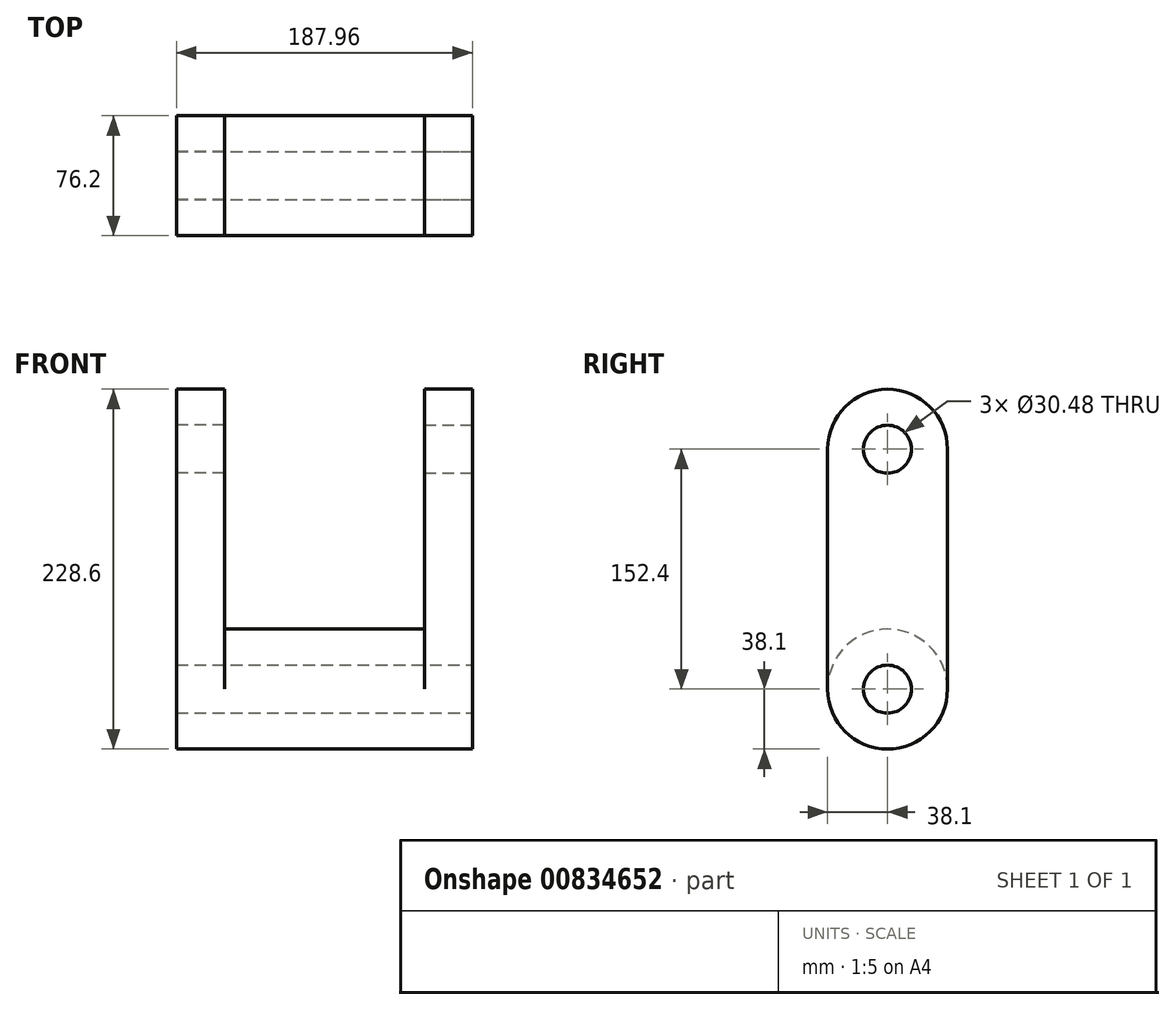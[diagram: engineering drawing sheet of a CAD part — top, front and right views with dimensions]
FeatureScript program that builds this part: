
annotation { "Feature Type Name" : "Feature", "Feature Type Description" : "" }
export const myFeature = defineFeature(function(context is Context, id is Id, definition is map)
    precondition{}
    {
        {
            var Q0;
            Q0=qCreatedBy(makeId("Right.planeOp"),FACE);
            var sketch = newSketch(context, id + "F0", { "sketchPlane" : qUnion([Q0])});
            skLineSegment(sketch, "E0.left", {"start": v(-38.1, 76.2) * mm, "end": v(-38.1, -76.2) * mm});
            skLineSegment(sketch, "E0.right", {"start": v(38.1, 76.2) * mm, "end": v(38.1, -76.2) * mm});
            skArc(sketch, "E1", {"start": v(38.1, 76.2) * mm, "mid": v(0, 114.3) * mm, "end": v(-38.1, 76.2) * mm});
            skArc(sketch, "E2", {"start": v(-38.1, -76.2) * mm, "mid": v(0, -114.3) * mm, "end": v(38.1, -76.2) * mm});
            skCircle(sketch, "E3", {"center": v(0, 76.2) * mm, "radius": 15.24 * mm});
            skCircle(sketch, "E4", {"center": v(0, -76.2) * mm, "radius": 15.24 * mm});
            skSolve(sketch);
        }
        {
            var Q0;
            Q0=makeQuery(id+"F0.imprint","IMPRINT",FACE,{"disambiguationData":[TD([[makeQuery(id+"F0.imprint","IMPRINT",EDGE,{"derivedFrom":sQuery(id+"F0.wireOp",EDGE,"E0.left")}),1.0]])]});
            extrude(context, id + "F1", {"entities" : qUnion([Q0]), "oppositeDirection" : true, "depth" : 30.48 * mm, "offsetDistance" : 25.4 * mm});
        }
        {
            var Q0;
            Q0=makeQuery(id+"F1.opExtrude","CAP_FACE",FACE,{"disambiguationData":[OSD([sQuery(id+"F0.wireOp",EDGE,"E0.left"),sQuery(id+"F0.wireOp",EDGE,"E0.right"),sQuery(id+"F0.wireOp",EDGE,"E1"),sQuery(id+"F0.wireOp",EDGE,"E2"),sQuery(id+"F0.wireOp",EDGE,"E3"),sQuery(id+"F0.wireOp",EDGE,"E4")])],"isStart":false});
            var sketch = newSketch(context, id + "F2", { "sketchPlane" : qUnion([Q0])});
            skCircle(sketch, "E5", {"center": v(0, -76.2) * mm, "radius": 38.1 * mm});
            skSolve(sketch);
        }
        {
            var Q0;
            {var subQ0=sQuery(id+"F2.wireOp",EDGE,"E5");Q0=makeQuery(id+"F2.imprint","IMPRINT",FACE,{"disambiguationData":[TD([[makeQuery(id+"F2.imprint","IMPRINT",EDGE,{"disambiguationData":[OD(0.0)],"derivedFrom":subQ0}),1.0]])]});}
            extrude(context, id + "F3", {"entities" : qUnion([Q0]), "operationType" : NewBodyOperationType.ADD, "depth" : 63.5 * mm, "offsetDistance" : 25.4 * mm});
        }
        {
            var Q0;
            Q0=qCreatedBy(makeId("Right.planeOp"),FACE);
            cPlane(context, id + "F4", {"entities" : qUnion([Q0]), "cplaneType" : CPlaneType.OFFSET, "offset" : 93.98 * mm, "oppositeDirection" : true, "width" : 152.4 * mm, "height" : 152.4 * mm});
        }
        {
            var Q0;
            Q0=makeQuery(id+"F1.opExtrude","SWEPT_BODY",BODY,{"disambiguationData":[OSD([sQuery(id+"F0.wireOp",EDGE,"E0.left"),sQuery(id+"F0.wireOp",EDGE,"E0.right"),sQuery(id+"F0.wireOp",EDGE,"E1"),sQuery(id+"F0.wireOp",EDGE,"E2"),sQuery(id+"F0.wireOp",EDGE,"E3"),sQuery(id+"F0.wireOp",EDGE,"E4")])]});
            var Q1;
            Q1=qCreatedBy(id+"F4.planeOp",FACE);
            mirror(context, id + "F5", {"operationType" : NewBodyOperationType.ADD, "entities" : qUnion([Q0]), "mirrorPlane" : qUnion([Q1])});
        }
    });
